# Revit family: З-ВО_Eng
name_source: partatom
category: Duct Accessories
units: mm (PartAtom-declared; Revit-internal decimal feet)

## family parameters
Always vertical = Yes
Cut with Voids When Loaded = No
Part Type = Attaches To
Round Connector Dimension = Use Diameter
Shared = No
Work Plane-Based = No

## types (11) — shared parameters
00_20_Manufacturer = Vents
00_20_Name = Hood
Casing Material = Metal, painted, blue, matte RAL 5007
Grid Material = Mesh, steel, painted,  RAL5007
Load Classification = HVAC
Maintenance zone material = <By Category>
Manufacturer = Vents
URL = https://ventilation-system.com
zero-valued in all types: Default Elevation

## per-type parameters (varying)
| type | A | A1 | D2 | Diameter | Dn | Dy | H | Height | Length | Weight | Width | a | a1 | h | h1 |
| Z-VO-400 | 612 mm | 490 mm  [stored 1.60761 ft] | 490 mm  [stored 1.60761 ft] | 400 mm  [stored 1.31234 ft] | 405 mm | 400 mm  [stored 1.31234 ft] | 319 mm  [stored 1.04659 ft] | 319 mm  [stored 1.04659 ft] | 707 mm | 10.00 kg | 612 mm | 353 mm | 283 mm | 150 mm | 85 mm |
| Z-VO-450 | 672 mm | 538 mm | 540 mm  [stored 1.77165 ft] | 450 mm  [stored 1.47638 ft] | 455 mm | 450 mm  [stored 1.47638 ft] | 319 mm  [stored 1.04659 ft] | 319 mm  [stored 1.04659 ft] | 776 mm | 11.00 kg | 672 mm | 388 mm | 310 mm | 150 mm | 85 mm |
| Z-VO-1250 | 1707 mm | 1366 mm | 1400 mm | 1250 mm | 1255 mm | 1250 mm | 685 mm | 685 mm | 1971 mm | 115.00 kg | 1707 mm | 986 mm | 788 mm | 285 mm  [stored 0.935039 ft] | 200 mm  [stored 0.656168 ft] |
| Z-VO-500 | 742 mm | 594 mm | 600 mm | 500 mm  [stored 1.64042 ft] | 505 mm  [stored 1.65682 ft] | 500 mm  [stored 1.64042 ft] | 350 mm  [stored 1.14829 ft] | 350 mm  [stored 1.14829 ft] | 857 mm | 14.00 kg | 742 mm | 428 mm | 343 mm  [stored 1.12533 ft] | 150 mm | 100 mm  [stored 0.328084 ft] |
| Z-VO-560 | 790 mm | 632 mm | 660 mm | 560 mm | 565 mm | 560 mm | 350 mm  [stored 1.14829 ft] | 350 mm  [stored 1.14829 ft] | 912 mm | 16.00 kg | 790 mm | 456 mm | 365 mm  [stored 1.19751 ft] | 150 mm | 100 mm  [stored 0.328084 ft] |
| Z-VO-630 | 860 mm | 688 mm | 730 mm | 630 mm | 635 mm | 630 mm | 359 mm  [stored 1.17782 ft] | 359 mm  [stored 1.17782 ft] | 993 mm | 20.00 kg | 860 mm | 497 mm | 397 mm | 150 mm | 105 mm  [stored 0.344488 ft] |
| Z-VO-710 | 988 mm | 790 mm | 810 mm | 710 mm | 715 mm | 710 mm | 420 mm  [stored 1.37795 ft] | 420 mm  [stored 1.37795 ft] | 1141 mm | 31.00 kg | 988 mm | 570 mm | 456 mm | 150 mm | 135 mm  [stored 0.442913 ft] |
| Z-VO-800 | 1072 mm | 858 mm | 900 mm | 800 mm | 805 mm | 800 mm | 475 mm  [stored 1.5584 ft] | 475 mm  [stored 1.5584 ft] | 1238 mm | 42.00 kg | 1072 mm | 619 mm | 495 mm | 190 mm | 143 mm |
| Z-VO-900 | 1189 mm | 951 mm | 1015 mm | 900 mm | 905 mm | 900 mm | 527 mm  [stored 1.729 ft] | 527 mm  [stored 1.729 ft] | 1373 mm | 57.00 kg | 1189 mm | 686 mm | 549 mm | 210 mm  [stored 0.688976 ft] | 159 mm |
| Z-VO-1000 | 1404 mm | 1123 mm | 1115 mm | 1000 mm | 1005 mm | 1000 mm | 640 mm | 640 mm | 1621 mm | 83.00 kg | 1404 mm | 811 mm | 648 mm | 240 mm  [stored 0.787402 ft] | 200 mm  [stored 0.656168 ft] |
| Z-VO-1120 | 1552 mm | 1242 mm | 1270 mm | 1120 mm | 1125 mm | 1120 mm | 655 mm | 655 mm | 1792 mm | 99.00 kg | 1552 mm | 896 mm | 717 mm | 255 mm  [stored 0.836614 ft] | 200 mm  [stored 0.656168 ft] |

note: column(s) folded — value = type name in every type: 00_20_Type

note: [stored X ft] marks values corroborated as IEEE doubles in the binary element streams (Revit-internal decimal feet)
